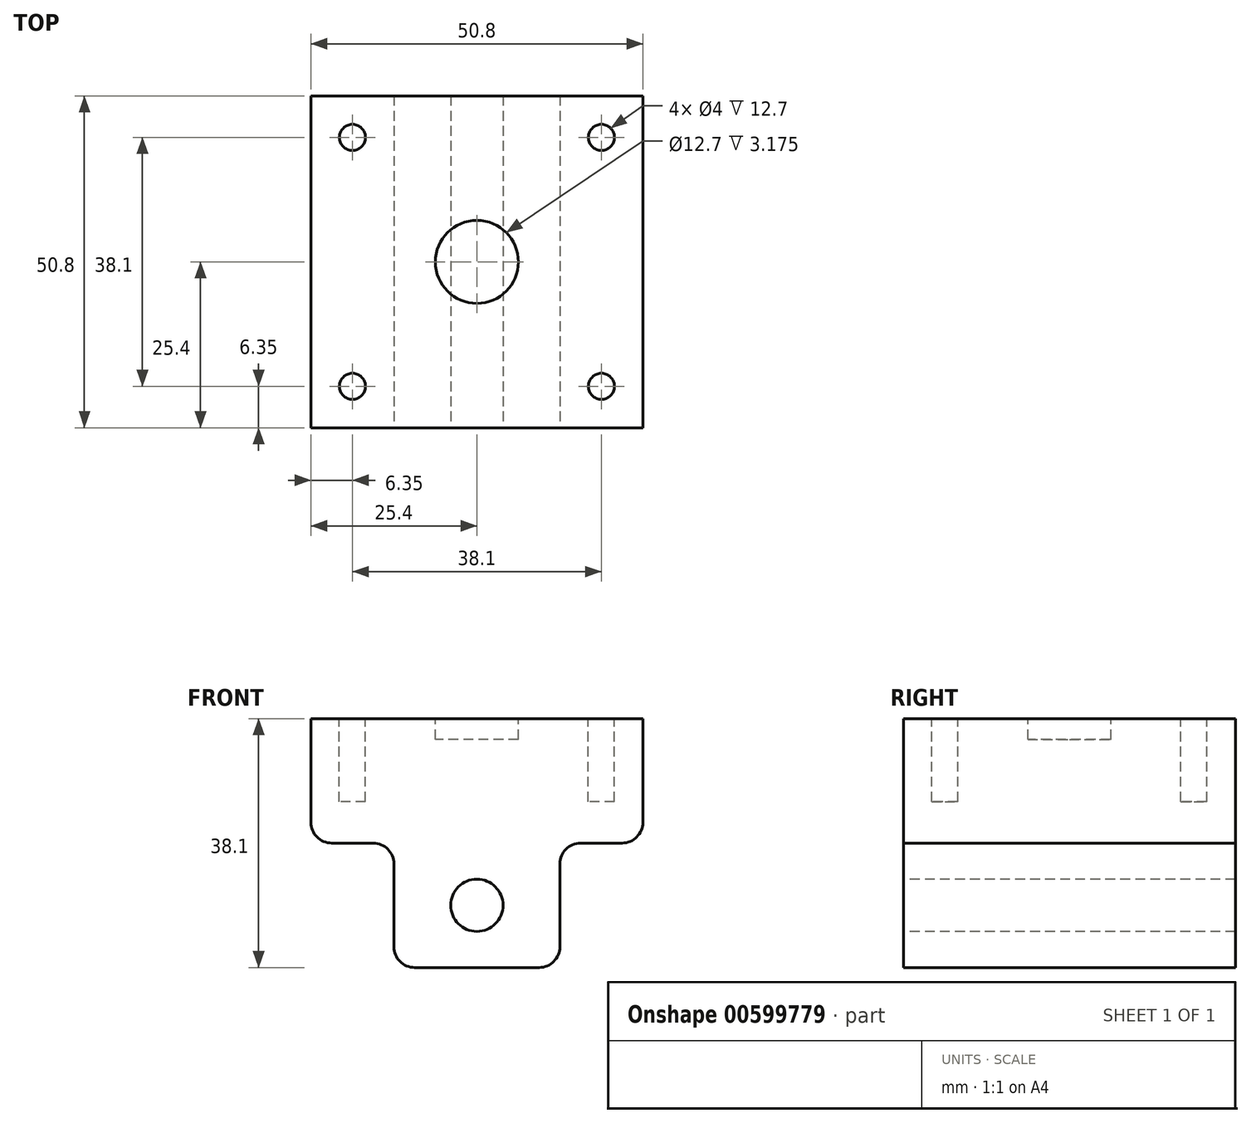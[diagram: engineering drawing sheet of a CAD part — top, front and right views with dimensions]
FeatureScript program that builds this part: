
annotation { "Feature Type Name" : "Feature", "Feature Type Description" : "" }
export const myFeature = defineFeature(function(context is Context, id is Id, definition is map)
    precondition{}
    {
        {
            var Q0;
            Q0=qCreatedBy(makeId("Front.planeOp"),FACE);
            var sketch = newSketch(context, id + "F0", { "sketchPlane" : qUnion([Q0])});
            skLineSegment(sketch, "E0", {"start": v(-25.4, 0) * mm, "end": v(25.4, 0) * mm});
            skLineSegment(sketch, "E1", {"start": v(25.4, 0) * mm, "end": v(25.4, -15.88) * mm});
            skLineSegment(sketch, "E2", {"start": v(22.23, -19.05) * mm, "end": v(15.88, -19.05) * mm});
            skLineSegment(sketch, "E3", {"start": v(12.7, -22.23) * mm, "end": v(12.7, -34.93) * mm});
            skLineSegment(sketch, "E4", {"start": v(9.53, -38.1) * mm, "end": v(-9.53, -38.1) * mm});
            skLineSegment(sketch, "E5", {"start": v(-12.7, -34.93) * mm, "end": v(-12.7, -22.23) * mm});
            skLineSegment(sketch, "E6", {"start": v(-15.88, -19.05) * mm, "end": v(-22.23, -19.05) * mm});
            skLineSegment(sketch, "E7", {"start": v(-25.4, -15.88) * mm, "end": v(-25.4, 0) * mm});
            skPoint(sketch, "E8.visualSharp", {"position": v(-12.7, -19.05) * mm});
            skArc(sketch, "E8.filletArc", {"start": v(-12.7, -22.23) * mm, "mid": v(-13.63, -19.98) * mm, "end": v(-15.88, -19.05) * mm});
            skPoint(sketch, "E9.visualSharp", {"position": v(12.7, -19.05) * mm});
            skArc(sketch, "E9.filletArc", {"start": v(15.88, -19.05) * mm, "mid": v(13.63, -19.98) * mm, "end": v(12.7, -22.23) * mm});
            skPoint(sketch, "E10.visualSharp", {"position": v(12.7, -38.1) * mm});
            skArc(sketch, "E10.filletArc", {"start": v(9.53, -38.1) * mm, "mid": v(11.77, -37.17) * mm, "end": v(12.7, -34.93) * mm});
            skPoint(sketch, "E11.visualSharp", {"position": v(-12.7, -38.1) * mm});
            skArc(sketch, "E11.filletArc", {"start": v(-12.7, -34.93) * mm, "mid": v(-11.77, -37.17) * mm, "end": v(-9.53, -38.1) * mm});
            skPoint(sketch, "E12.visualSharp", {"position": v(-25.4, -19.05) * mm});
            skArc(sketch, "E12.filletArc", {"start": v(-25.4, -15.88) * mm, "mid": v(-24.47, -18.12) * mm, "end": v(-22.23, -19.05) * mm});
            skPoint(sketch, "E13.visualSharp", {"position": v(25.4, -19.05) * mm});
            skArc(sketch, "E13.filletArc", {"start": v(22.23, -19.05) * mm, "mid": v(24.47, -18.12) * mm, "end": v(25.4, -15.88) * mm});
            skCircle(sketch, "E14", {"center": v(0, -28.58) * mm, "radius": 4 * mm});
            skPoint(sketch, "E14.centerSnap0", {"position": v(12.7, -28.58) * mm});
            skPoint(sketch, "E14.centerSnap1", {"position": v(0, -38.1) * mm});
            skSolve(sketch);
        }
        {
            var Q0;
            Q0 = qSketchRegion(id + "F0", true);
            extrude(context, id + "F1", {"entities" : qUnion([Q0]), "endBound" : BoundingType.SYMMETRIC, "oppositeDirection" : true, "depth" : 50.8 * mm, "offsetDistance" : 25.4 * mm});
        }
        {
            var Q0;
            Q0=makeQuery(id+"F1.opExtrude","SWEPT_FACE",FACE,{"disambiguationData":[OSD([sQuery(id+"F0.wireOp",EDGE,"E0")])]});
            var sketch = newSketch(context, id + "F2", { "sketchPlane" : qUnion([Q0])});
            skCircle(sketch, "E15", {"center": v(-19.05, -19.05) * mm, "radius": 2 * mm});
            skLineSegment(sketch, "E16", {"start": v(-25.4, 0) * mm, "end": v(25.4, 0) * mm, "construction": true});
            skLineSegment(sketch, "E17", {"start": v(-19.05, -19.05) * mm, "end": v(-19.05, -25.4) * mm, "construction": true});
            skLineSegment(sketch, "E18", {"start": v(-19.05, -19.05) * mm, "end": v(-25.4, -19.05) * mm, "construction": true});
            skCircle(sketch, "E19.1.0", {"center": v(19.05, -19.05) * mm, "radius": 2 * mm});
            skCircle(sketch, "E19.2.0", {"center": v(19.05, 19.05) * mm, "radius": 2 * mm});
            skCircle(sketch, "E19.3.0", {"center": v(-19.05, 19.05) * mm, "radius": 2 * mm});
            skPoint(sketch, "E19.center", {"position": v(0, 0) * mm});
            skSolve(sketch);
        }
        {
            var Q0;
            Q0 = qSketchRegion(id + "F2", true);
            extrude(context, id + "F3", {"entities" : qUnion([Q0]), "operationType" : NewBodyOperationType.REMOVE, "oppositeDirection" : true, "depth" : 12.7 * mm, "offsetDistance" : 25.4 * mm});
        }
        {
            var Q0;
            Q0=makeQuery(id+"F1.opExtrude","SWEPT_FACE",FACE,{"disambiguationData":[OSD([sQuery(id+"F0.wireOp",EDGE,"E0")])]});
            var sketch = newSketch(context, id + "F4", { "sketchPlane" : qUnion([Q0])});
            skCircle(sketch, "E20", {"center": v(0, 0) * mm, "radius": 6.35 * mm});
            skSolve(sketch);
        }
        {
            var Q0;
            Q0 = qSketchRegion(id + "F4", true);
            extrude(context, id + "F5", {"entities" : qUnion([Q0]), "operationType" : NewBodyOperationType.REMOVE, "oppositeDirection" : true, "depth" : 3.17 * mm, "offsetDistance" : 25.4 * mm});
        }
    });
